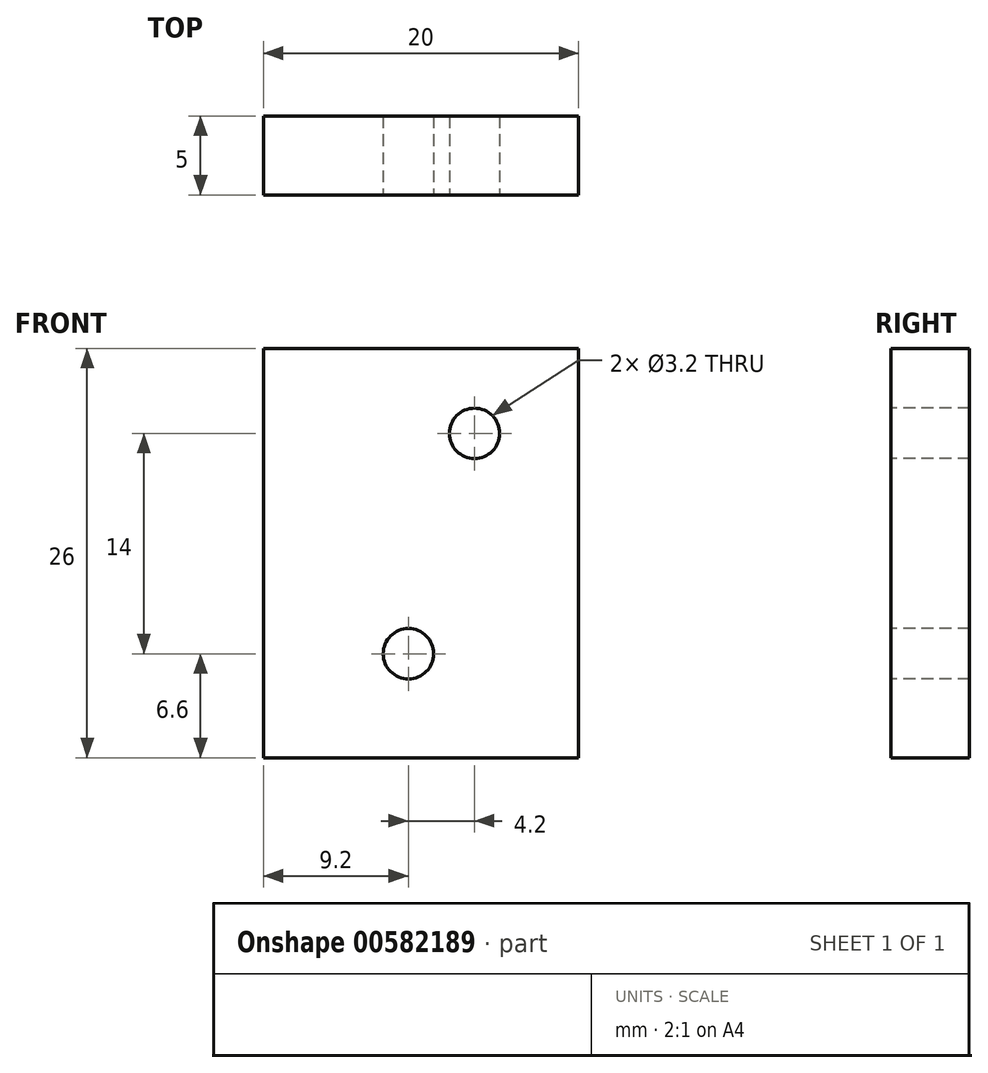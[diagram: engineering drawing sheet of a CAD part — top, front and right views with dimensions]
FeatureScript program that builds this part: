
annotation { "Feature Type Name" : "Feature", "Feature Type Description" : "" }
export const myFeature = defineFeature(function(context is Context, id is Id, definition is map)
    precondition{}
    {
        {
            var Q0;
            Q0=qCreatedBy(makeId("Front.planeOp"),FACE);
            var sketch = newSketch(context, id + "F0", { "sketchPlane" : qUnion([Q0])});
            skLineSegment(sketch, "E0.bottom", {"start": v(0, 0) * mm, "end": v(20, 0) * mm});
            skLineSegment(sketch, "E0.top", {"start": v(0, -26) * mm, "end": v(20, -26) * mm});
            skLineSegment(sketch, "E0.left", {"start": v(0, 0) * mm, "end": v(0, -26) * mm});
            skLineSegment(sketch, "E0.right", {"start": v(20, 0) * mm, "end": v(20, -26) * mm});
            skSolve(sketch);
        }
        {
            var Q0;
            Q0=makeQuery(id+"F0.imprint","IMPRINT",FACE,{"disambiguationData":[TD([[makeQuery(id+"F0.imprint","IMPRINT",EDGE,{"derivedFrom":sQuery(id+"F0.wireOp",EDGE,"E0.bottom")}),-1.0]])]});
            extrude(context, id + "F1", {"entities" : qUnion([Q0]), "depth" : 5 * mm, "offsetDistance" : 25 * mm});
        }
        {
            var Q0;
            Q0=makeQuery(id+"F1.opExtrude","CAP_FACE",FACE,{"disambiguationData":[OSD([sQuery(id+"F0.wireOp",EDGE,"E0.bottom"),sQuery(id+"F0.wireOp",EDGE,"E0.top"),sQuery(id+"F0.wireOp",EDGE,"E0.left"),sQuery(id+"F0.wireOp",EDGE,"E0.right")])],"isStart":false});
            var sketch = newSketch(context, id + "F2", { "sketchPlane" : qUnion([Q0])});
            skCircle(sketch, "E1", {"center": v(13.4, -5.4) * mm, "radius": 1.6 * mm});
            skCircle(sketch, "E2", {"center": v(9.2, -19.4) * mm, "radius": 1.6 * mm});
            skSolve(sketch);
        }
        {
            var Q0;
            Q0=makeQuery(id+"F2.imprint","IMPRINT",FACE,{"disambiguationData":[TD([[makeQuery(id+"F2.imprint","IMPRINT",EDGE,{"derivedFrom":sQuery(id+"F2.wireOp",EDGE,"E2")}),1.0]])]});
            var Q1;
            Q1=makeQuery(id+"F2.imprint","IMPRINT",FACE,{"disambiguationData":[TD([[makeQuery(id+"F2.imprint","IMPRINT",EDGE,{"derivedFrom":sQuery(id+"F2.wireOp",EDGE,"E1")}),1.0]])]});
            extrude(context, id + "F3", {"entities" : qUnion([Q0, Q1]), "operationType" : NewBodyOperationType.REMOVE, "endBound" : BoundingType.THROUGH_ALL, "oppositeDirection" : true, "depth" : 25 * mm, "offsetDistance" : 25 * mm});
        }
    });
